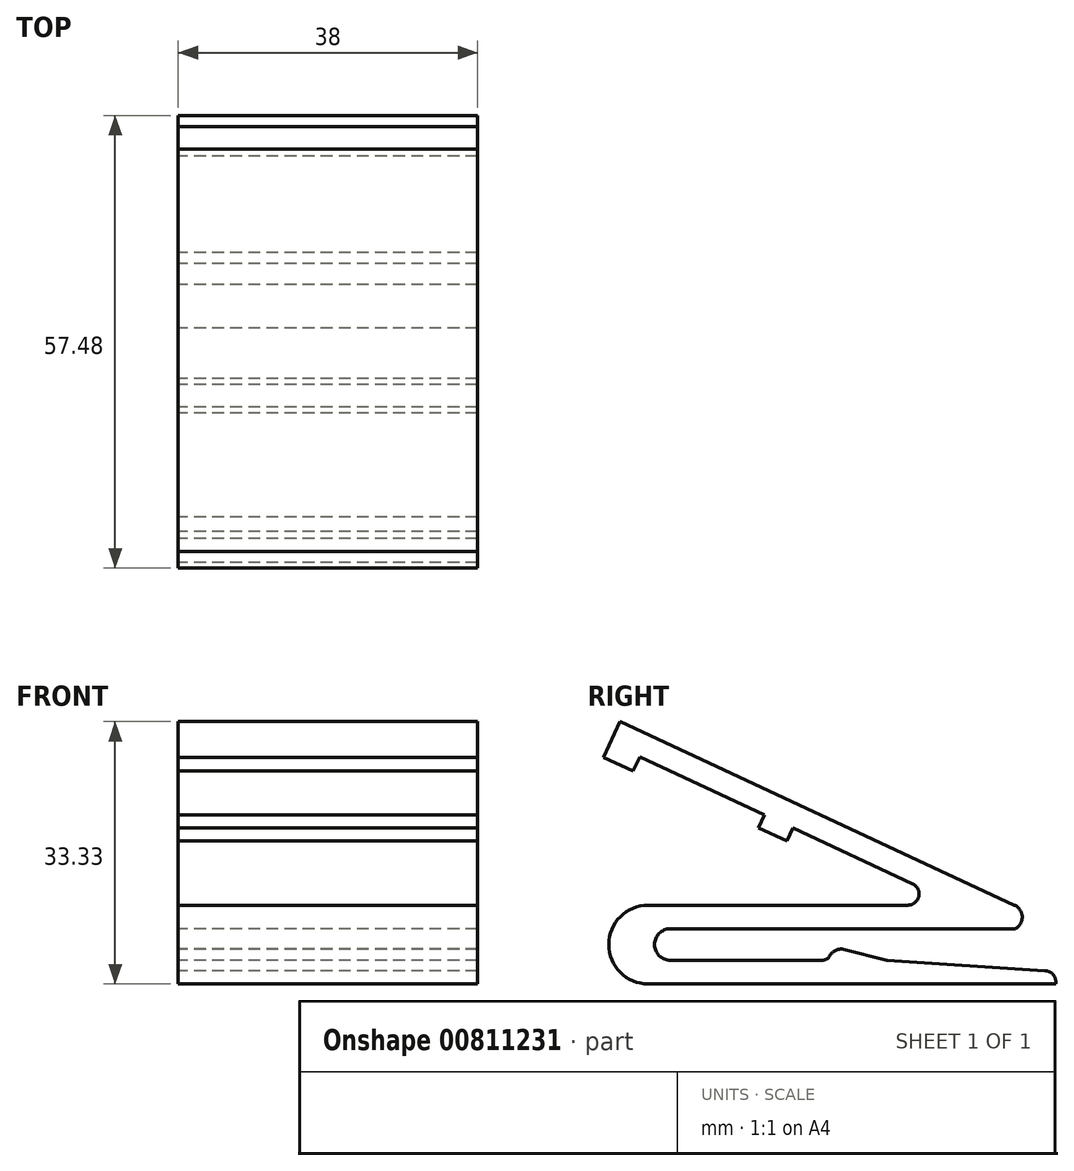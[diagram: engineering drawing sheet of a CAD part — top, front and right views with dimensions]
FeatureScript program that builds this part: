
annotation { "Feature Type Name" : "Feature", "Feature Type Description" : "" }
export const myFeature = defineFeature(function(context is Context, id is Id, definition is map)
    precondition{}
    {
        {
            var Q0;
            Q0=qCreatedBy(makeId("Right.planeOp"),FACE);
            var sketch = newSketch(context, id + "F0", { "sketchPlane" : qUnion([Q0])});
            skLineSegment(sketch, "E0", {"start": v(-26.95, 30.67) * mm, "end": v(23.18, 7.34) * mm});
            skLineSegment(sketch, "E1", {"start": v(-26.95, 30.67) * mm, "end": v(-29.06, 26.14) * mm});
            skLineSegment(sketch, "E2", {"start": v(-29.06, 26.14) * mm, "end": v(-25.28, 24.38) * mm});
            skLineSegment(sketch, "E3", {"start": v(-25.28, 24.38) * mm, "end": v(-24.44, 26.2) * mm});
            skLineSegment(sketch, "E4", {"start": v(-24.44, 26.2) * mm, "end": v(10.2, 10.07) * mm});
            skLineSegment(sketch, "E5", {"start": v(9.62, 7.34) * mm, "end": v(-23.38, 7.34) * mm});
            skLineSegment(sketch, "E6", {"start": v(23.24, 4.34) * mm, "end": v(-20.56, 4.34) * mm});
            skLineSegment(sketch, "E7", {"start": v(-20.56, 0.34) * mm, "end": v(6.96, 0.34) * mm});
            skLineSegment(sketch, "E8", {"start": v(-23.38, -2.66) * mm, "end": v(28.4, -2.66) * mm});
            skLineSegment(sketch, "E9", {"start": v(27.05, -0.99) * mm, "end": v(6.96, 0.34) * mm});
            skArc(sketch, "E10", {"start": v(9.62, 7.34) * mm, "mid": v(11, 8.48) * mm, "end": v(10.2, 10.07) * mm});
            skArc(sketch, "E11", {"start": v(28.4, -2.66) * mm, "mid": v(28.1, -1.52) * mm, "end": v(27.05, -0.99) * mm});
            skArc(sketch, "E12", {"start": v(-23.38, 7.34) * mm, "mid": v(-28.38, 2.34) * mm, "end": v(-23.38, -2.66) * mm});
            skArc(sketch, "E13", {"start": v(-20.56, 4.34) * mm, "mid": v(-22.56, 2.34) * mm, "end": v(-20.56, 0.34) * mm});
            skLineSegment(sketch, "E14", {"start": v(-8.6, 18.82) * mm, "end": v(-9.36, 17.2) * mm});
            skLineSegment(sketch, "E15", {"start": v(-9.36, 17.2) * mm, "end": v(-5.73, 15.5) * mm});
            skLineSegment(sketch, "E16", {"start": v(-5.73, 15.5) * mm, "end": v(-4.98, 17.13) * mm});
            skArc(sketch, "E17", {"start": v(23.24, 4.34) * mm, "mid": v(24.14, 5.86) * mm, "end": v(23.18, 7.34) * mm});
            skLineSegment(sketch, "E18", {"start": v(6.96, 0.34) * mm, "end": v(1.46, 1.73) * mm});
            skFitSpline(sketch, "E19", {"points": [v(1.46, 1.73) * mm, v(0.81, 1.73) * mm, v(0.4, 1.6) * mm, v(0.07, 1.38) * mm, v(-0.23, 1.01) * mm, v(-0.39, 0.76) * mm, v(-0.6, 0.56) * mm, v(-0.83, 0.42) * mm, v(-1.38, 0.34) * mm], "startDerivative": vector(-6.05, 1.03) * mm, "endDerivative": vector(-6.36, 0) * mm});
            skSolve(sketch);
        }
        {
            var Q0;
            Q0 = qSketchRegion(id + "F0", true);
            extrude(context, id + "F1", {"entities" : qUnion([Q0]), "depth" : 38 * mm, "offsetDistance" : 25 * mm});
        }
    });
